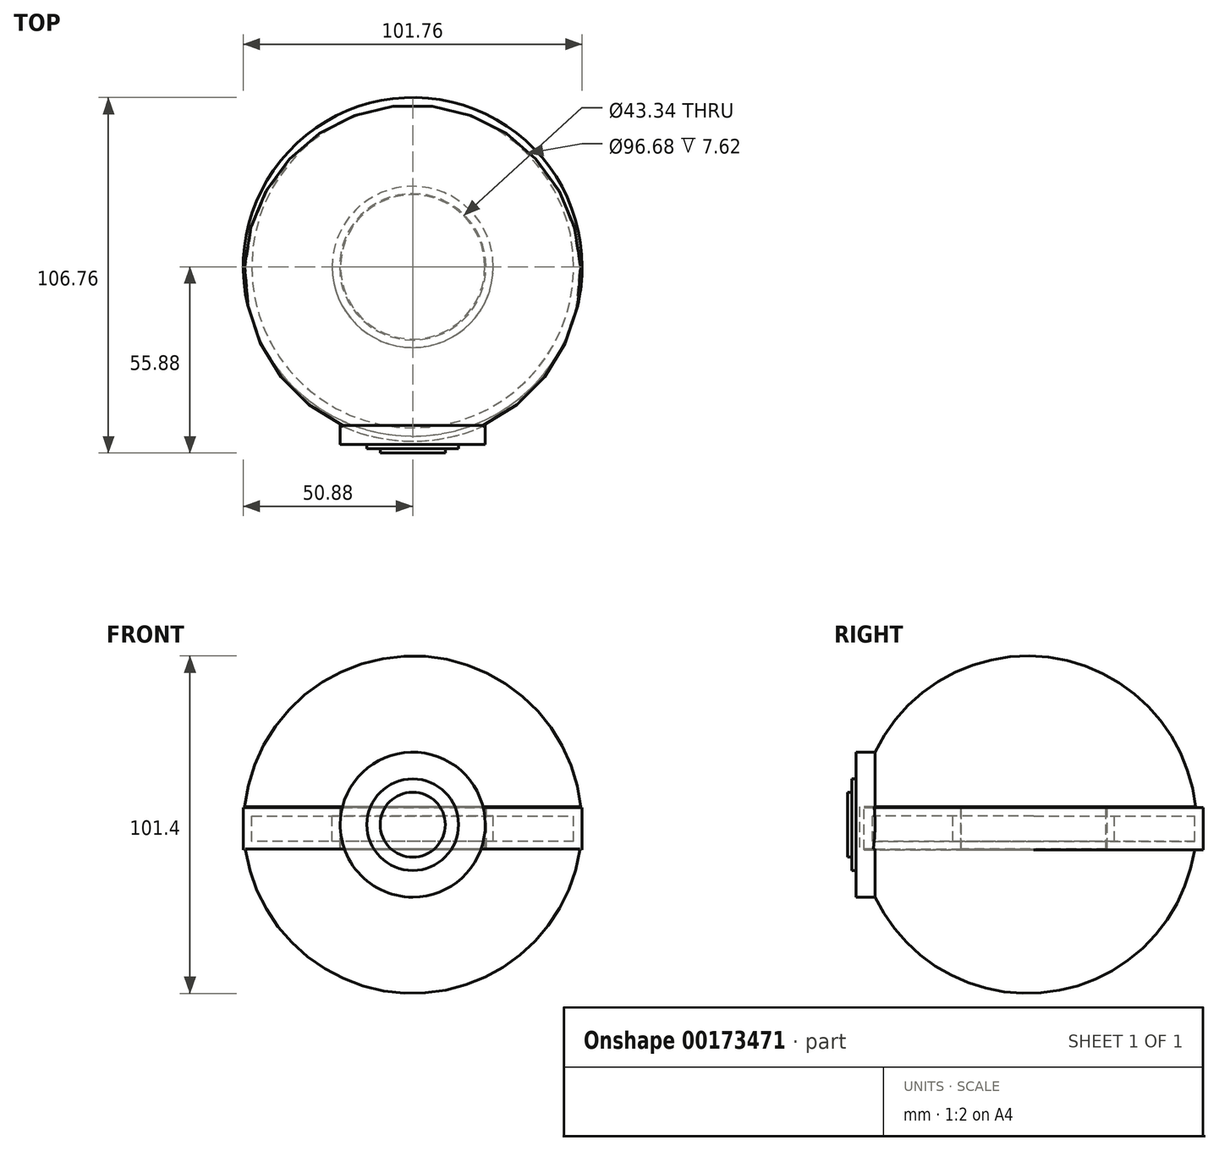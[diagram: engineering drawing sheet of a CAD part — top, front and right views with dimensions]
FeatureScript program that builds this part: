
annotation { "Feature Type Name" : "Feature", "Feature Type Description" : "" }
export const myFeature = defineFeature(function(context is Context, id is Id, definition is map)
    precondition{}
    {
        {
            var Q0;
            Q0=qCreatedBy(makeId("Top.planeOp"),FACE);
            var sketch = newSketch(context, id + "F0", { "sketchPlane" : qUnion([Q0])});
            skArc(sketch, "E0", {"start": v(-50.8, -1.8) * mm, "mid": v(0, -52.5) * mm, "end": v(50.8, -1.81) * mm});
            skLineSegment(sketch, "E1", {"start": v(-50.8, -1.8) * mm, "end": v(50.8, -1.81) * mm});
            skSolve(sketch);
        }
        {
            var Q0;
            Q0=makeQuery(id+"F0.imprint","IMPRINT",FACE,{"disambiguationData":[TD([[makeQuery(id+"F0.imprint","IMPRINT",EDGE,{"derivedFrom":sQuery(id+"F0.wireOp",EDGE,"E0")}),1.0]])]});
            var Q1;
            Q1=sQuery(id+"F0.wireOp",EDGE,"E1");
            revolve(context, id + "F1", {"entities" : qUnion([Q0]), "axis" : qUnion([Q1]), "revolveType" : RevolveType.FULL});
        }
        {
            var Q0;
            Q0=qCreatedBy(makeId("Front.planeOp"),FACE);
            var sketch = newSketch(context, id + "F2", { "sketchPlane" : qUnion([Q0])});
            skCircle(sketch, "E2", {"center": v(0, 0) * mm, "radius": 13.77 * mm});
            skSolve(sketch);
        }
        {
            var Q0;
            Q0 = qSketchRegion(id + "F2", true);
            extrude(context, id + "F3", {"entities" : qUnion([Q0]), "operationType" : NewBodyOperationType.ADD, "depth" : 54.6 * mm});
        }
        {
            var Q0;
            Q0=qCreatedBy(makeId("Front.planeOp"),FACE);
            var sketch = newSketch(context, id + "F4", { "sketchPlane" : qUnion([Q0])});
            skCircle(sketch, "E3", {"center": v(0, 0) * mm, "radius": 9.76 * mm});
            skSolve(sketch);
        }
        {
            var Q0;
            Q0 = qSketchRegion(id + "F4", true);
            extrude(context, id + "F5", {"entities" : qUnion([Q0]), "operationType" : NewBodyOperationType.ADD, "depth" : 55.88 * mm});
        }
        {
            var Q0;
            Q0=qCreatedBy(makeId("Front.planeOp"),FACE);
            var sketch = newSketch(context, id + "F6", { "sketchPlane" : qUnion([Q0])});
            skCircle(sketch, "E4", {"center": v(0, 0) * mm, "radius": 21.78 * mm});
            skSolve(sketch);
        }
        {
            var Q0;
            Q0=qCreatedBy(makeId("Front.planeOp"),FACE);
            var sketch = newSketch(context, id + "F7", { "sketchPlane" : qUnion([Q0])});
            skLineSegment(sketch, "E5", {"start": v(-21.98, 5.37) * mm, "end": v(-52.37, 5.37) * mm});
            skLineSegment(sketch, "E6", {"start": v(-21.98, -7.33) * mm, "end": v(-52.37, -7.33) * mm});
            skLineSegment(sketch, "E7", {"start": v(-52.37, 5.37) * mm, "end": v(-52.37, -7.33) * mm});
            skLineSegment(sketch, "E8", {"start": v(-21.98, -7.33) * mm, "end": v(-21.98, 5.37) * mm});
            skSolve(sketch);
        }
        {
            var Q0;
            Q0 = qSketchRegion(id + "F6", true);
            extrude(context, id + "F8", {"entities" : qUnion([Q0]), "operationType" : NewBodyOperationType.ADD, "depth" : 53.34 * mm});
        }
        {
            var Q0;
            Q0=qCreatedBy(makeId("Front.planeOp"),FACE);
            var sketch = newSketch(context, id + "F9", { "sketchPlane" : qUnion([Q0])});
            skArc(sketch, "E9", {"start": v(-56.21, 0.73) * mm, "mid": v(-0.17, -56.22) * mm, "end": v(56.22, 0.39) * mm});
            skLineSegment(sketch, "E10", {"start": v(-56.21, 0.73) * mm, "end": v(56.22, 0.39) * mm});
            skLineSegment(sketch, "E11", {"start": v(0, 6.1) * mm, "end": v(0, -7.12) * mm});
            skSolve(sketch);
        }
        {
            var Q0;
            Q0 = qSketchRegion(id + "F7", true);
            var Q1;
            Q1=sQuery(id+"F9.wireOp",EDGE,"E11");
            revolve(context, id + "F10", {"operationType" : NewBodyOperationType.REMOVE, "entities" : qUnion([Q0]), "axis" : qUnion([Q1]), "revolveType" : RevolveType.FULL, "oppositeDirection" : true});
        }
        {
            var Q0;
            Q0=qCreatedBy(makeId("Front.planeOp"),FACE);
            var sketch = newSketch(context, id + "F11", { "sketchPlane" : qUnion([Q0])});
            skLineSegment(sketch, "E12", {"start": v(-21.67, 5.15) * mm, "end": v(-21.67, -7.55) * mm});
            skLineSegment(sketch, "E13", {"start": v(-21.67, -7.55) * mm, "end": v(-50.88, -7.55) * mm});
            skLineSegment(sketch, "E14", {"start": v(-50.88, -7.55) * mm, "end": v(-50.88, 5.15) * mm});
            skLineSegment(sketch, "E15", {"start": v(-50.88, 5.15) * mm, "end": v(-21.67, 5.15) * mm});
            skLineSegment(sketch, "E16", {"start": v(0, 6.18) * mm, "end": v(0, -8.24) * mm});
            skSolve(sketch);
        }
        {
            var Q0;
            Q0=makeQuery(id+"F11.imprint","IMPRINT",FACE,{"disambiguationData":[TD([[makeQuery(id+"F11.imprint","IMPRINT",EDGE,{"derivedFrom":sQuery(id+"F11.wireOp",EDGE,"E12")}),-1.0]])]});
            var Q1;
            Q1=sQuery(id+"F11.wireOp",EDGE,"E16");
            revolve(context, id + "F12", {"entities" : qUnion([Q0]), "axis" : qUnion([Q1]), "revolveType" : RevolveType.FULL});
        }
        {
            var Q0;
            Q0=makeQuery(id+"F12.opRevolve","SWEPT_FACE",FACE,{"disambiguationData":[OSD([sQuery(id+"F11.wireOp",EDGE,"E14")])]});
            var Q1;
            Q1=makeQuery(id+"F12.opRevolve","SWEPT_BODY",BODY,{"disambiguationData":[OSD([sQuery(id+"F11.wireOp",EDGE,"E12"),sQuery(id+"F11.wireOp",EDGE,"E13"),sQuery(id+"F11.wireOp",EDGE,"E14"),sQuery(id+"F11.wireOp",EDGE,"E15")])]});
            shell(context, id + "F13", {"isHollow" : true, "entities" : qUnion([Q0]), "parts" : qUnion([Q1]), "thickness" : 2.54 * mm});
        }
    });
